# Revit family: 0044182 Feilo Sylvania Lighting Fixture OPTIX R 625 3L 4K ALU EMCB
name_source: partatom
category: Lighting Fixtures
revit_build: Autodesk Revit 2017 (Build: 20190507_1515(x64)
units: mm (PartAtom-declared; Revit-internal decimal feet)

## family parameters
Cut with Voids When Loaded = No
Host = Face
Light Source = No
OmniClass Number = 23.80.70.00
OmniClass Title = Lighting
Part Type = Normal
Room Calculation Point = No
Round Connector Dimension = Use Diameter
Shared = No

## types (1)
- 0044182 OPTIX R 625 3L 4K ALU EMCB
    Apparent Load = 26 VA
    Assembly Code = D5020200
    AssetType = Fixed
    ClassificationName = Uniclass2015
    ClassificationValue = EF_70_80
    Cost = 0 $
    Default Elevation = 1219 mm
    Description = OPTIX RECESSED 625x625 3L 4000K ALU EMCB is a high efficacy low glare luminaire for office and education applications. Ceiling recessed 625x625 mm. White plastic low glare optics in 3 lines configuration. White RAL9016 fixture body. Constant current driver. Suitable for central battery DC emergency operation. 4000K Neutral White LED, CRI>80, chromaticity tolerance of 3-step MacAdam ellipse. Luminous flux 3450lm. Power consumption 24W. Luminaire efficacy 144lm/W. Lumen maintenance of L90B50 > 72000h, L90B10 = 46000h. UGR<19, IK07, IP20. Photobiological safety risk group 0. Electrical protection Class I. Glow wire test 650°C.
    DocumentationLiterature = http://www.sylvania-lighting.com
    DurationUnit = hours
    ElectricShockClassification = Class I
    ExpectedLife = 50000
    Height = 38 mm  [stored 0.124672 ft]
    IfcExportAs = IfcLightFixtureType
    IfcExportType = IfcLightFixtureType
    ImpactProtectionIndex = IK07
    IngressProtection = IP20
    InputNominalFrequency = 50/60 Hz
    InputVoltage = 220-240V~
    Keynote = 16500
    Lamp = LED
    LampColourRenderingIndex = 80
    LampColourTemperature = 4000 K
    LampMacAdamStep = 3
    LampNominalLuminous = 3600 lm
    LampsType = LED
    Length = 621 mm  [stored 2.0374 ft]
    LuminousEfficacy = 138 lm/W
    Manufacturer = Feilo Sylvania
    ManufacturerName = Feilo Sylvania
    Material = steel housing, polycarbonate diffuser
    Material_1_FEILO = <By Category>
    Material_2_FEILO = <By Category>
    Material_3_FEILO = <By Category>
    Material_4_FEILO = <By Category>
    Model = OPTIX R 625 3L 4K ALU EMCB
    ModelNumber = 0044182
    ModelReference = OPTIX R 625 3L 4K ALU EMCB
    Name = OPTIX R 625 3L 4K ALU EMCB
    NominalDepth = 621 mm  [stored 2.0374 ft]
    NominalHeight = 38 mm  [stored 0.124672 ft]
    NominalLength = 621 mm  [stored 2.0374 ft]
    PowerConsumption = 26 W
    PowerFactor = 0.95
    Type Image = <None>
    TypeName = OPTIX R 625 3L 4K ALU EMCB
    URL = http://www.sylvania-lighting.com
    Voltage = 230 V
    Weight = 5.0 kg
    Width = 621 mm  [stored 2.0374 ft]

note: [stored X ft] marks values corroborated as IEEE doubles in the binary element streams (Revit-internal decimal feet)

## geometry (parser evidence)
native form markers: Sweep x6
no freeform markers — native parametric forms only
